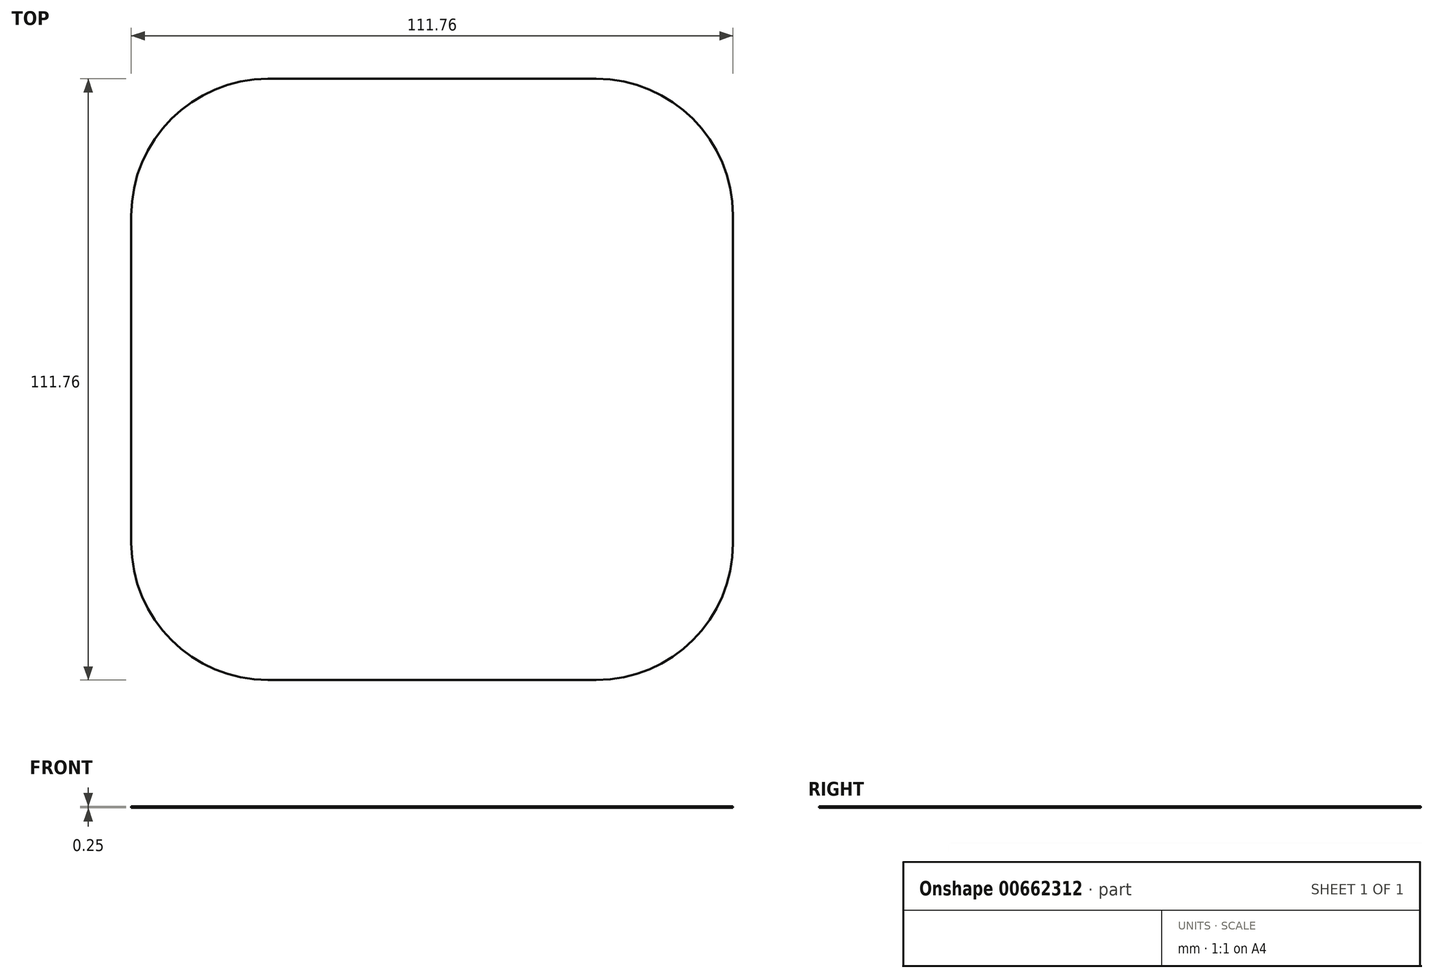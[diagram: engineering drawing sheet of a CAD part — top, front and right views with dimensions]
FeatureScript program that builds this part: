
annotation { "Feature Type Name" : "Feature", "Feature Type Description" : "" }
export const myFeature = defineFeature(function(context is Context, id is Id, definition is map)
    precondition{}
    {
        {
            var Q0;
            Q0=qCreatedBy(makeId("Top.planeOp"),FACE);
            var sketch = newSketch(context, id + "F0", { "sketchPlane" : qUnion([Q0])});
            skLineSegment(sketch, "E0.bottom", {"start": v(30.48, 55.88) * mm, "end": v(-30.48, 55.88) * mm});
            skLineSegment(sketch, "E0.top", {"start": v(30.48, -55.88) * mm, "end": v(-30.48, -55.88) * mm});
            skLineSegment(sketch, "E0.left", {"start": v(55.88, 30.48) * mm, "end": v(55.88, -30.48) * mm});
            skLineSegment(sketch, "E0.right", {"start": v(-55.88, 30.48) * mm, "end": v(-55.88, -30.48) * mm});
            skPoint(sketch, "E0.middle", {"position": v(0, 0) * mm});
            skPoint(sketch, "E1.visualSharp", {"position": v(-55.88, 55.88) * mm});
            skArc(sketch, "E1.filletArc", {"start": v(-30.48, 55.88) * mm, "mid": v(-48.44, 48.44) * mm, "end": v(-55.88, 30.48) * mm});
            skPoint(sketch, "E2.visualSharp", {"position": v(55.88, 55.88) * mm});
            skArc(sketch, "E2.filletArc", {"start": v(55.88, 30.48) * mm, "mid": v(48.44, 48.44) * mm, "end": v(30.48, 55.88) * mm});
            skPoint(sketch, "E3.visualSharp", {"position": v(55.88, -55.88) * mm});
            skArc(sketch, "E3.filletArc", {"start": v(30.48, -55.88) * mm, "mid": v(48.44, -48.44) * mm, "end": v(55.88, -30.48) * mm});
            skPoint(sketch, "E4.visualSharp", {"position": v(-55.88, -55.88) * mm});
            skArc(sketch, "E4.filletArc", {"start": v(-55.88, -30.48) * mm, "mid": v(-48.44, -48.44) * mm, "end": v(-30.48, -55.88) * mm});
            skSolve(sketch);
        }
        {
            var Q0;
            Q0 = qSketchRegion(id + "F0", true);
            extrude(context, id + "F1", {"entities" : qUnion([Q0]), "depth" : 0.25 * mm, "offsetDistance" : 25.4 * mm});
        }
    });
